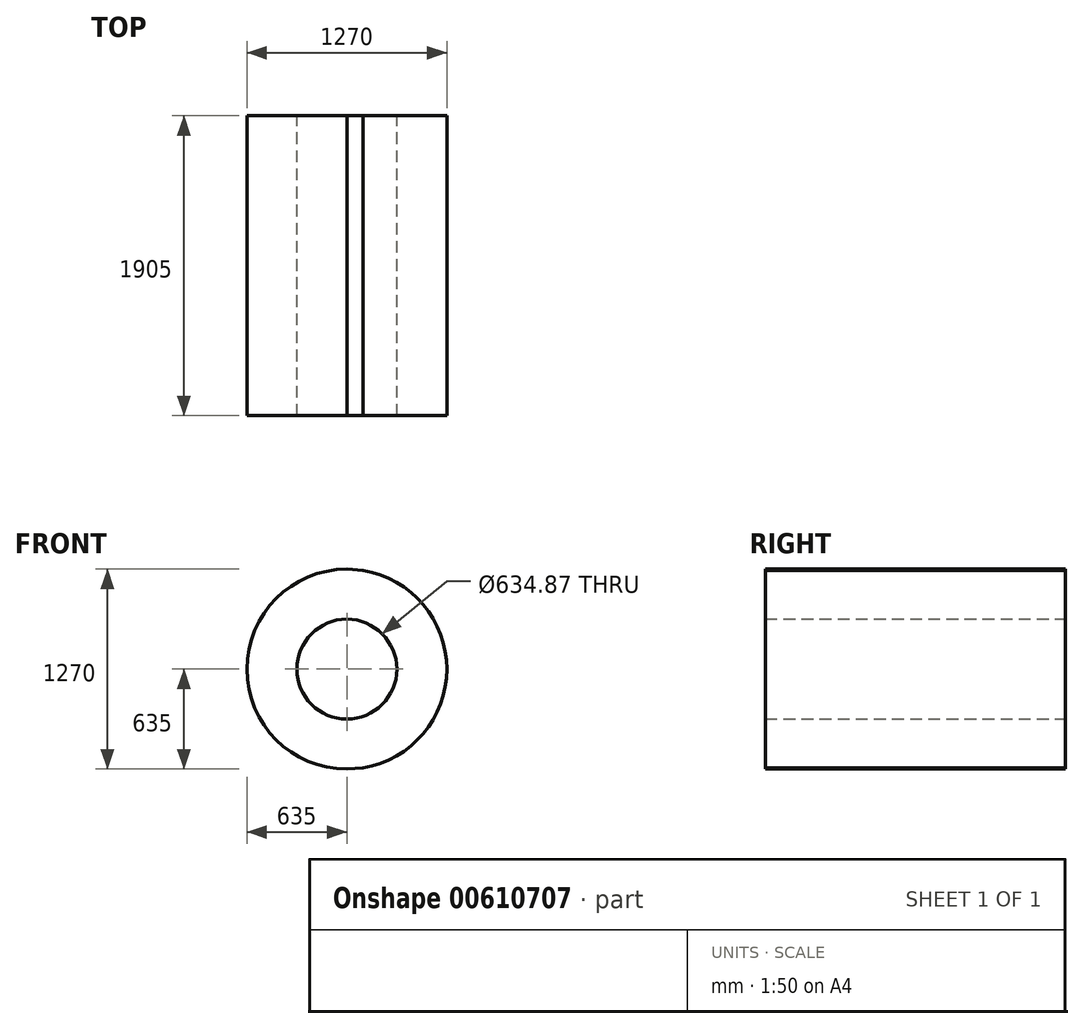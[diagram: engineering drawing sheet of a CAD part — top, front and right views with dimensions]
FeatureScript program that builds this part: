
annotation { "Feature Type Name" : "Feature", "Feature Type Description" : "" }
export const myFeature = defineFeature(function(context is Context, id is Id, definition is map)
    precondition{}
    {
        {
            var Q0;
            Q0=qCreatedBy(makeId("Front.planeOp"),FACE);
            var sketch = newSketch(context, id + "F0", { "sketchPlane" : qUnion([Q0])});
            skCircle(sketch, "E0", {"center": v(0, 0) * mm, "radius": 635 * mm});
            skCircle(sketch, "E1", {"center": v(2286, 0) * mm, "radius": 444.5 * mm});
            skLineSegment(sketch, "E2", {"start": v(0, 635) * mm, "end": v(2322.62, 442.99) * mm});
            skLineSegment(sketch, "E3", {"start": v(0, -635) * mm, "end": v(2322.62, -442.99) * mm});
            skCircle(sketch, "E4", {"center": v(0, 0) * mm, "radius": 317.43 * mm});
            skCircle(sketch, "E5", {"center": v(2286, 0) * mm, "radius": 164 * mm});
            skSolve(sketch);
        }
        {
            var Q0;
            Q0=makeQuery(id+"F0.imprint","IMPRINT",FACE,{"disambiguationData":[TD([[makeQuery(id+"F0.imprint","IMPRINT",EDGE,{"derivedFrom":sQuery(id+"F0.wireOp",EDGE,"E4")}),-1.0]])]});
            extrude(context, id + "F1", {"entities" : qUnion([Q0]), "depth" : 635 * mm, "offsetDistance" : 25.4 * mm});
        }
        {
            var Q0;
            Q0=makeQuery(id+"F1.opExtrude","CAP_FACE",FACE,{"disambiguationData":[OSD([sQuery(id+"F0.wireOp",EDGE,"E0"),sQuery(id+"F0.wireOp",EDGE,"E2"),sQuery(id+"F0.wireOp",EDGE,"E3"),sQuery(id+"F0.wireOp",EDGE,"E4")])],"isStart":false});
            extrude(context, id + "F2", {"entities" : qUnion([Q0]), "operationType" : NewBodyOperationType.ADD, "depth" : 1270 * mm, "offsetDistance" : 25.4 * mm});
        }
    });
